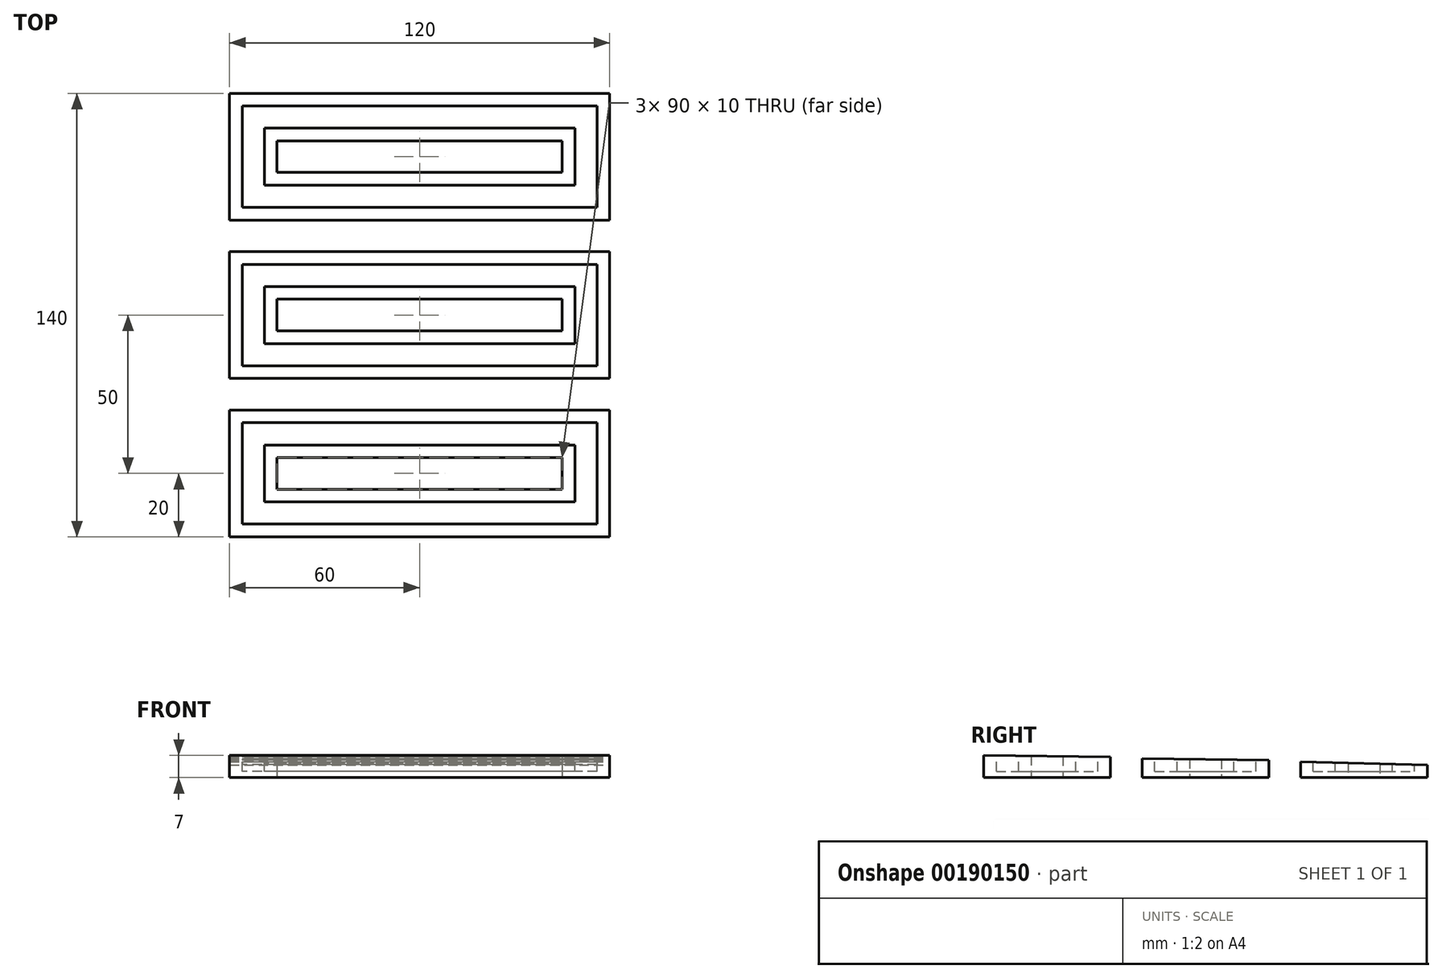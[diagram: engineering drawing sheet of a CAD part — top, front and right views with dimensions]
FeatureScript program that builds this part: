
annotation { "Feature Type Name" : "Feature", "Feature Type Description" : "" }
export const myFeature = defineFeature(function(context is Context, id is Id, definition is map)
    precondition{}
    {
        {
            var Q0;
            Q0=qCreatedBy(makeId("Top.planeOp"),FACE);
            var sketch = newSketch(context, id + "F0", { "sketchPlane" : qUnion([Q0])});
            skLineSegment(sketch, "E0.bottom", {"start": v(60, -20) * mm, "end": v(-60, -20) * mm});
            skLineSegment(sketch, "E0.top", {"start": v(60, 20) * mm, "end": v(-60, 20) * mm});
            skLineSegment(sketch, "E0.left", {"start": v(60, -20) * mm, "end": v(60, 20) * mm});
            skLineSegment(sketch, "E0.right", {"start": v(-60, -20) * mm, "end": v(-60, 20) * mm});
            skPoint(sketch, "E0.middle", {"position": v(0, 0) * mm});
            skLineSegment(sketch, "E1.0", {"start": v(45, -5) * mm, "end": v(45, 5) * mm});
            skLineSegment(sketch, "E1.1", {"start": v(45, -5) * mm, "end": v(-45, -5) * mm});
            skLineSegment(sketch, "E1.2", {"start": v(-45, -5) * mm, "end": v(-45, 5) * mm});
            skLineSegment(sketch, "E1.3", {"start": v(45, 5) * mm, "end": v(-45, 5) * mm});
            skLineSegment(sketch, "E2.0.1.0", {"start": v(60, 30) * mm, "end": v(60, 70) * mm});
            skLineSegment(sketch, "E2.0.1.1", {"start": v(45, 45) * mm, "end": v(-45, 45) * mm});
            skLineSegment(sketch, "E2.0.1.2", {"start": v(-45, 45) * mm, "end": v(-45, 55) * mm});
            skLineSegment(sketch, "E2.0.1.3", {"start": v(60, 30) * mm, "end": v(-60, 30) * mm});
            skLineSegment(sketch, "E2.0.1.4", {"start": v(45, 55) * mm, "end": v(-45, 55) * mm});
            skLineSegment(sketch, "E2.0.1.5", {"start": v(-60, 30) * mm, "end": v(-60, 70) * mm});
            skLineSegment(sketch, "E2.0.1.6", {"start": v(45, 45) * mm, "end": v(45, 55) * mm});
            skLineSegment(sketch, "E2.0.1.7", {"start": v(60, 70) * mm, "end": v(-60, 70) * mm});
            skPoint(sketch, "E2.0.1.8", {"position": v(0, 50) * mm});
            skLineSegment(sketch, "E2.0.2.0", {"start": v(60, 80) * mm, "end": v(60, 120) * mm});
            skLineSegment(sketch, "E2.0.2.1", {"start": v(45, 95) * mm, "end": v(-45, 95) * mm});
            skLineSegment(sketch, "E2.0.2.2", {"start": v(-45, 95) * mm, "end": v(-45, 105) * mm});
            skLineSegment(sketch, "E2.0.2.3", {"start": v(60, 80) * mm, "end": v(-60, 80) * mm});
            skLineSegment(sketch, "E2.0.2.4", {"start": v(45, 105) * mm, "end": v(-45, 105) * mm});
            skLineSegment(sketch, "E2.0.2.5", {"start": v(-60, 80) * mm, "end": v(-60, 120) * mm});
            skLineSegment(sketch, "E2.0.2.6", {"start": v(45, 95) * mm, "end": v(45, 105) * mm});
            skLineSegment(sketch, "E2.0.2.7", {"start": v(60, 120) * mm, "end": v(-60, 120) * mm});
            skPoint(sketch, "E2.0.2.8", {"position": v(0, 100) * mm});
            skLineSegment(sketch, "E2.direction1", {"start": v(-60, -20) * mm, "end": v(70, -20) * mm, "construction": true});
            skLineSegment(sketch, "E2.direction2", {"start": v(-60, -20) * mm, "end": v(-60, 30) * mm, "construction": true});
            skSolve(sketch);
        }
        {
            var Q0;
            Q0=qSketchRegion(id+"F0",true);
            extrude(context, id + "F1", {"entities" : qUnion([Q0]), "depth" : 7 * mm, "offsetDistance" : 25 * mm});
        }
        {
            var Q0;
            Q0=makeQuery(id+"F1.opExtrude","CAP_FACE",FACE,{"disambiguationData":[OSD([sQuery(id+"F0.wireOp",EDGE,"E0.bottom"),sQuery(id+"F0.wireOp",EDGE,"E0.top"),sQuery(id+"F0.wireOp",EDGE,"E0.left"),sQuery(id+"F0.wireOp",EDGE,"E0.right"),sQuery(id+"F0.wireOp",EDGE,"E1.0"),sQuery(id+"F0.wireOp",EDGE,"E1.1"),sQuery(id+"F0.wireOp",EDGE,"E1.2"),sQuery(id+"F0.wireOp",EDGE,"E1.3")])],"isStart":false});
            var sketch = newSketch(context, id + "F2", { "sketchPlane" : qUnion([Q0])});
            skLineSegment(sketch, "E3.0", {"start": v(56, 16) * mm, "end": v(-56, 16) * mm});
            skLineSegment(sketch, "E3.1", {"start": v(56, -16) * mm, "end": v(56, 16) * mm});
            skLineSegment(sketch, "E3.2", {"start": v(56, -16) * mm, "end": v(-56, -16) * mm});
            skLineSegment(sketch, "E3.3", {"start": v(-56, -16) * mm, "end": v(-56, 16) * mm});
            skLineSegment(sketch, "E4.0", {"start": v(49, 9) * mm, "end": v(-49, 9) * mm});
            skLineSegment(sketch, "E4.1", {"start": v(49, -9) * mm, "end": v(49, 9) * mm});
            skLineSegment(sketch, "E4.2", {"start": v(49, -9) * mm, "end": v(-49, -9) * mm});
            skLineSegment(sketch, "E4.3", {"start": v(-49, -9) * mm, "end": v(-49, 9) * mm});
            skSolve(sketch);
        }
        {
            var Q0;
            Q0 = qSketchRegion(id + "F2", true);
            extrude(context, id + "F3", {"entities" : qUnion([Q0]), "operationType" : NewBodyOperationType.REMOVE, "oppositeDirection" : true, "depth" : 5 * mm, "offsetDistance" : 25 * mm});
        }
        {
            var Q0;
            Q0=makeQuery(id+"F1.opExtrude","CAP_FACE",FACE,{"disambiguationData":[OSD([sQuery(id+"F0.wireOp",EDGE,"E2.0.1.0"),sQuery(id+"F0.wireOp",EDGE,"E2.0.1.1"),sQuery(id+"F0.wireOp",EDGE,"E2.0.1.2"),sQuery(id+"F0.wireOp",EDGE,"E2.0.1.3"),sQuery(id+"F0.wireOp",EDGE,"E2.0.1.4"),sQuery(id+"F0.wireOp",EDGE,"E2.0.1.5"),sQuery(id+"F0.wireOp",EDGE,"E2.0.1.6"),sQuery(id+"F0.wireOp",EDGE,"E2.0.1.7")])],"isStart":false});
            var sketch = newSketch(context, id + "F4", { "sketchPlane" : qUnion([Q0])});
            skLineSegment(sketch, "E5.0", {"start": v(56, 66) * mm, "end": v(-56, 66) * mm});
            skLineSegment(sketch, "E5.1", {"start": v(56, 34) * mm, "end": v(56, 66) * mm});
            skLineSegment(sketch, "E5.2", {"start": v(56, 34) * mm, "end": v(-56, 34) * mm});
            skLineSegment(sketch, "E5.3", {"start": v(-56, 34) * mm, "end": v(-56, 66) * mm});
            skLineSegment(sketch, "E6.0", {"start": v(49, 59) * mm, "end": v(-49, 59) * mm});
            skLineSegment(sketch, "E6.1", {"start": v(49, 41) * mm, "end": v(49, 59) * mm});
            skLineSegment(sketch, "E6.2", {"start": v(49, 41) * mm, "end": v(-49, 41) * mm});
            skLineSegment(sketch, "E6.3", {"start": v(-49, 41) * mm, "end": v(-49, 59) * mm});
            skSolve(sketch);
        }
        {
            var Q0;
            Q0 = qSketchRegion(id + "F4", true);
            extrude(context, id + "F5", {"entities" : qUnion([Q0]), "operationType" : NewBodyOperationType.REMOVE, "oppositeDirection" : true, "depth" : 5 * mm, "offsetDistance" : 25 * mm});
        }
        {
            var Q0;
            Q0=makeQuery(id+"F1.opExtrude","CAP_FACE",FACE,{"disambiguationData":[OSD([sQuery(id+"F0.wireOp",EDGE,"E2.0.2.0"),sQuery(id+"F0.wireOp",EDGE,"E2.0.2.1"),sQuery(id+"F0.wireOp",EDGE,"E2.0.2.2"),sQuery(id+"F0.wireOp",EDGE,"E2.0.2.3"),sQuery(id+"F0.wireOp",EDGE,"E2.0.2.4"),sQuery(id+"F0.wireOp",EDGE,"E2.0.2.5"),sQuery(id+"F0.wireOp",EDGE,"E2.0.2.6"),sQuery(id+"F0.wireOp",EDGE,"E2.0.2.7")])],"isStart":false});
            var sketch = newSketch(context, id + "F6", { "sketchPlane" : qUnion([Q0])});
            skLineSegment(sketch, "E7.0", {"start": v(56, 116) * mm, "end": v(-56, 116) * mm});
            skLineSegment(sketch, "E7.1", {"start": v(56, 84) * mm, "end": v(56, 116) * mm});
            skLineSegment(sketch, "E7.2", {"start": v(56, 84) * mm, "end": v(-56, 84) * mm});
            skLineSegment(sketch, "E7.3", {"start": v(-56, 84) * mm, "end": v(-56, 116) * mm});
            skLineSegment(sketch, "E8.0", {"start": v(49, 109) * mm, "end": v(-49, 109) * mm});
            skLineSegment(sketch, "E8.1", {"start": v(49, 91) * mm, "end": v(49, 109) * mm});
            skLineSegment(sketch, "E8.2", {"start": v(49, 91) * mm, "end": v(-49, 91) * mm});
            skLineSegment(sketch, "E8.3", {"start": v(-49, 91) * mm, "end": v(-49, 109) * mm});
            skSolve(sketch);
        }
        {
            var Q0;
            Q0 = qSketchRegion(id + "F6", true);
            extrude(context, id + "F7", {"entities" : qUnion([Q0]), "operationType" : NewBodyOperationType.REMOVE, "oppositeDirection" : true, "depth" : 5 * mm, "offsetDistance" : 25 * mm});
        }
        {
            var Q0;
            Q0=makeQuery(id+"F1.opExtrude","SWEPT_FACE",FACE,{"disambiguationData":[OSD([sQuery(id+"F0.wireOp",EDGE,"E0.left")])]});
            var sketch = newSketch(context, id + "F8", { "sketchPlane" : qUnion([Q0])});
            skLineSegment(sketch, "E9", {"start": v(-20, 7) * mm, "end": v(20, 6.5) * mm});
            skLineSegment(sketch, "E10", {"start": v(20, 6.5) * mm, "end": v(20, 7) * mm});
            skLineSegment(sketch, "E11", {"start": v(20, 7) * mm, "end": v(-20, 7) * mm});
            skSolve(sketch);
        }
        {
            var Q0;
            Q0 = qSketchRegion(id + "F8", true);
            extrude(context, id + "F9", {"entities" : qUnion([Q0]), "operationType" : NewBodyOperationType.REMOVE, "endBound" : BoundingType.THROUGH_ALL, "oppositeDirection" : true, "depth" : 25 * mm, "offsetDistance" : 25 * mm});
        }
        {
            var Q0;
            Q0=makeQuery(id+"F1.opExtrude","SWEPT_FACE",FACE,{"disambiguationData":[OSD([sQuery(id+"F0.wireOp",EDGE,"E2.0.1.0")])]});
            var sketch = newSketch(context, id + "F10", { "sketchPlane" : qUnion([Q0])});
            skLineSegment(sketch, "E12", {"start": v(30, 6) * mm, "end": v(70, 5.5) * mm});
            skLineSegment(sketch, "E13", {"start": v(70, 5.5) * mm, "end": v(70, 7) * mm});
            skLineSegment(sketch, "E14", {"start": v(70, 7) * mm, "end": v(30, 7) * mm});
            skLineSegment(sketch, "E15", {"start": v(30, 7) * mm, "end": v(30, 6) * mm});
            skSolve(sketch);
        }
        {
            var Q0;
            Q0 = qSketchRegion(id + "F10", true);
            extrude(context, id + "F11", {"entities" : qUnion([Q0]), "operationType" : NewBodyOperationType.REMOVE, "endBound" : BoundingType.THROUGH_ALL, "oppositeDirection" : true, "depth" : 25 * mm, "offsetDistance" : 25 * mm});
        }
        {
            var Q0;
            Q0=makeQuery(id+"F1.opExtrude","SWEPT_FACE",FACE,{"disambiguationData":[OSD([sQuery(id+"F0.wireOp",EDGE,"E2.0.2.0")])]});
            var sketch = newSketch(context, id + "F12", { "sketchPlane" : qUnion([Q0])});
            skLineSegment(sketch, "E16", {"start": v(80, 5) * mm, "end": v(120, 4) * mm});
            skLineSegment(sketch, "E17", {"start": v(120, 4) * mm, "end": v(120, 7) * mm});
            skLineSegment(sketch, "E18", {"start": v(120, 7) * mm, "end": v(80, 7) * mm});
            skLineSegment(sketch, "E19", {"start": v(80, 7) * mm, "end": v(80, 5) * mm});
            skSolve(sketch);
        }
        {
            var Q0;
            Q0 = qSketchRegion(id + "F12", true);
            extrude(context, id + "F13", {"entities" : qUnion([Q0]), "operationType" : NewBodyOperationType.REMOVE, "endBound" : BoundingType.THROUGH_ALL, "oppositeDirection" : true, "depth" : 25 * mm, "offsetDistance" : 25 * mm});
        }
    });
